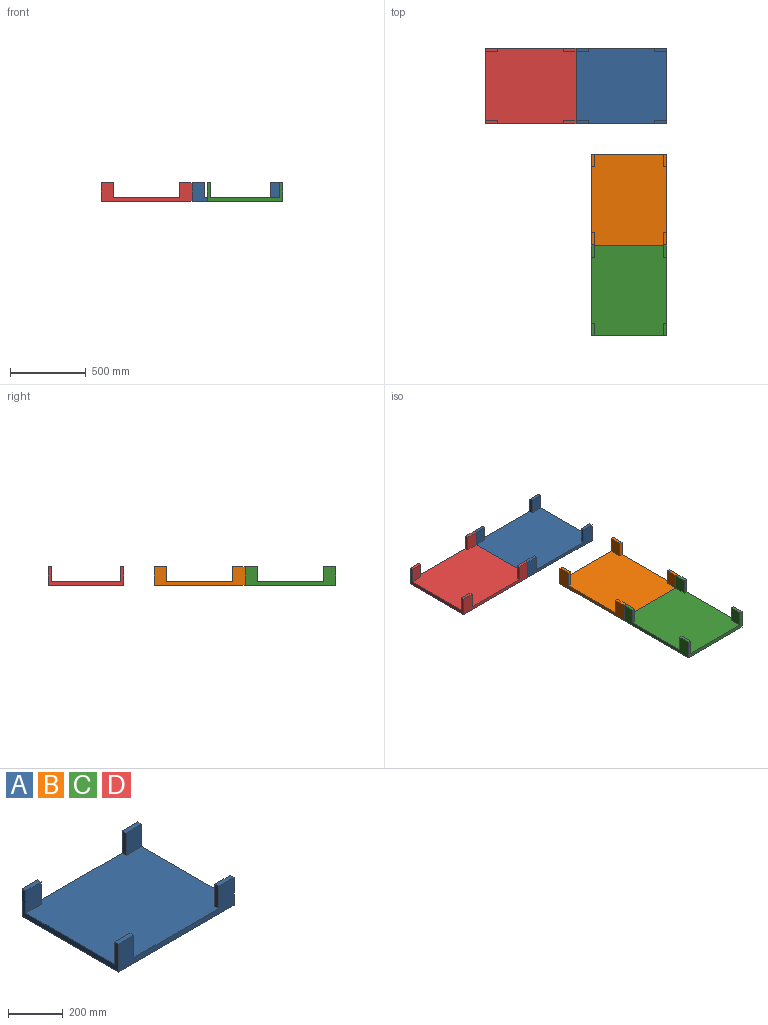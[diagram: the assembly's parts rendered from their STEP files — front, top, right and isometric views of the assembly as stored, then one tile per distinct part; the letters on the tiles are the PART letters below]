
ASSEMBLY  parts=4 mates=5
PART A: 18 faces, bbox 600x500x125 mm
  f0: plane 600x500mm, normal (0,0,1), area 293600mm2, adj f1,f2,f3,f4,f6,f7,f9,f10
  f1: plane 600x125mm, normal (0,1,0), area 31000mm2, adj f0,f2,f4,f5,f7,f8,f9,f11
  f2: plane 500x125mm, normal (-1,0,0), area 16500mm2, adj f0,f1,f3,f5,f6,f8,f12,f14
  f3: plane 600x125mm, normal (0,-1,0), area 31000mm2, adj f0,f2,f4,f5,f13,f14,f16,f17
  f4: plane 500x125mm, normal (1,0,0), area 16500mm2, adj f0,f1,f3,f5,f10,f11,f15,f17
  f5: plane 600x500mm, normal (0,0,-1), area 300000mm2, adj f1,f2,f3,f4
  f6: plane 100x80mm, normal (0,-1,0), area 8000mm2, adj f0,f2,f7,f8
  f7: plane 100x20mm, normal (1,0,0), area 2000mm2, adj f0,f1,f6,f8
  f8: plane 80x20mm, normal (0,0,1), area 1600mm2, adj f1,f2,f6,f7
  f9: plane 100x20mm, normal (-1,0,0), area 2000mm2, adj f0,f1,f10,f11
  f10: plane 100x80mm, normal (0,-1,0), area 8000mm2, adj f0,f4,f9,f11
  f11: plane 80x20mm, normal (0,0,1), area 1600mm2, adj f1,f4,f9,f10
  f12: plane 100x80mm, normal (0,1,0), area 8000mm2, adj f0,f2,f13,f14
  f13: plane 100x20mm, normal (1,0,0), area 2000mm2, adj f0,f3,f12,f14
  f14: plane 80x20mm, normal (0,0,1), area 1600mm2, adj f2,f3,f12,f13
  f15: plane 100x80mm, normal (0,1,0), area 8000mm2, adj f0,f4,f16,f17
  f16: plane 100x20mm, normal (-1,0,0), area 2000mm2, adj f0,f3,f15,f17
  f17: plane 80x20mm, normal (0,0,1), area 1600mm2, adj f3,f4,f15,f16
PART B: same geometry as A
PART C: same geometry as A
PART D: same geometry as A
PLACE A t=(435.49,1064.51,227)mm
PLACE B rot(axis=(0,0,-1),90deg) t=(491.24,320.26,227)mm
PLACE C rot(axis=(0,0,-1),90deg) t=(491.24,-279.74,227)mm
PLACE D t=(-164.51,1064.51,227)mm
MATE planar C.f2 <-> B.f4  axis (0,1,0) through (491.24,14.51,254.65)mm
MATE fastened C.f5 <-> B.f5  axis (0,0,1) through (241.24,14.51,227)mm
MATE planar D.f4 <-> A.f2  axis (1,0,0) through (141.24,1064.51,254.65)mm
MATE fastened A.f5 <-> D.f5  axis (0,0,1) through (141.24,814.51,227)mm
MATE fastened A.f5 <-> C.f5  axis (0,0,1) through (741.24,814.51,227)mm
